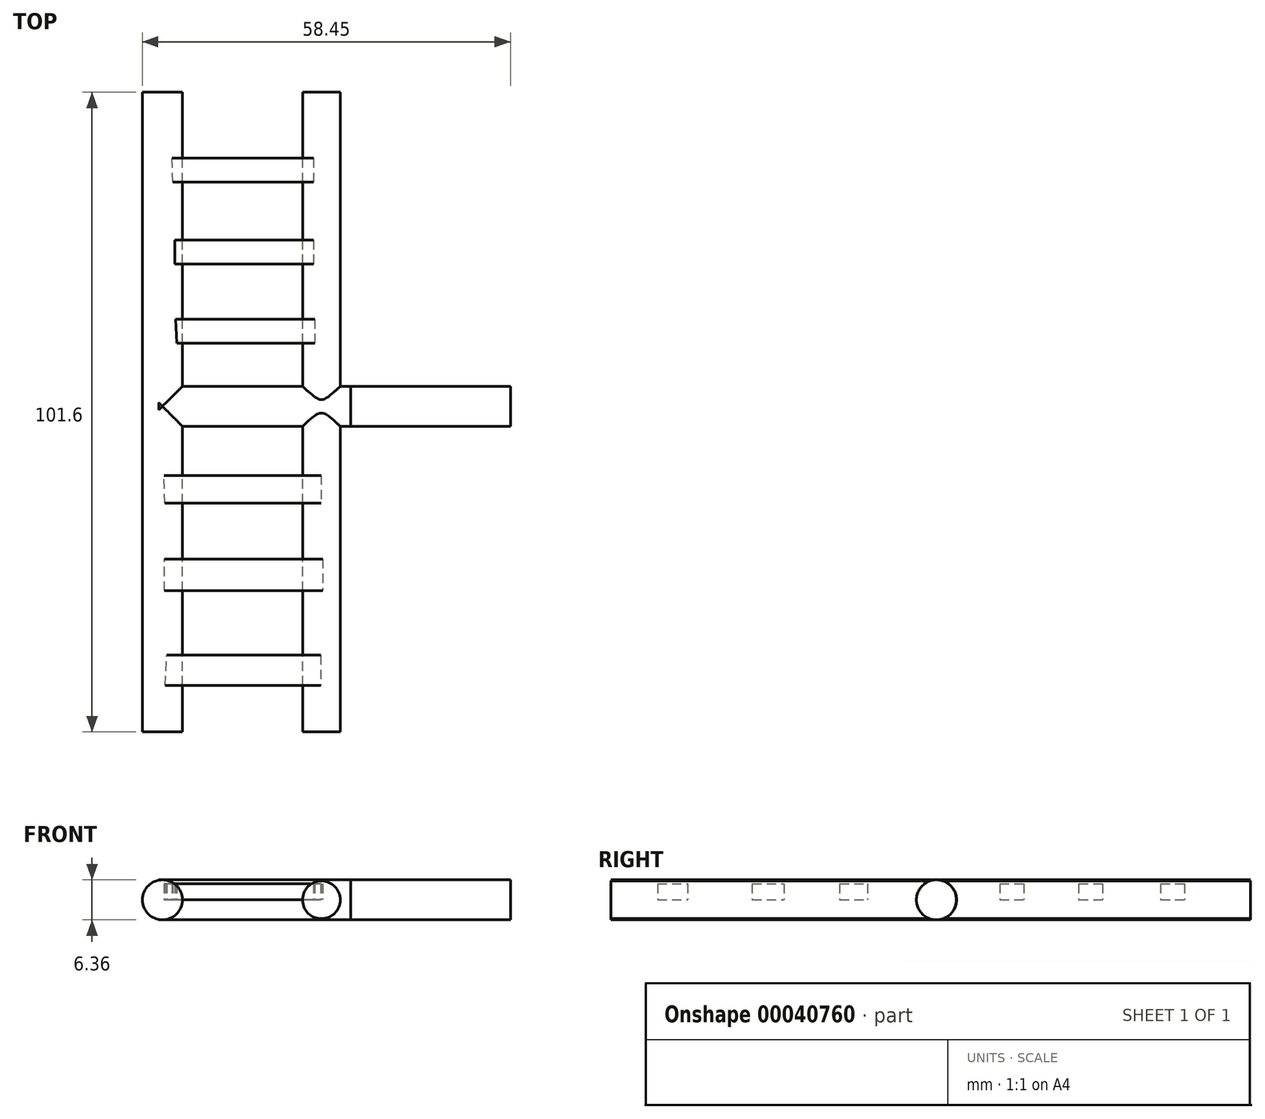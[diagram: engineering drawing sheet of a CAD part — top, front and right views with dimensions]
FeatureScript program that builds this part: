
annotation { "Feature Type Name" : "Feature", "Feature Type Description" : "" }
export const myFeature = defineFeature(function(context is Context, id is Id, definition is map)
    precondition{}
    {
        {
            var Q0;
            Q0=qCreatedBy(makeId("Front.planeOp"),FACE);
            var sketch = newSketch(context, id + "F0", { "sketchPlane" : qUnion([Q0])});
            skCircle(sketch, "E0", {"center": v(-29.87, 0) * mm, "radius": 3.18 * mm});
            skCircle(sketch, "E1", {"center": v(-4.62, 0) * mm, "radius": 3 * mm});
            skLineSegment(sketch, "E2", {"start": v(-26.7, 0) * mm, "end": v(-7.61, 0) * mm});
            skSolve(sketch);
        }
        {
            var Q0;
            Q0=makeQuery(id+"F0.imprint","IMPRINT",FACE,{"disambiguationData":[TD([[makeQuery(id+"F0.imprint","IMPRINT",EDGE,{"derivedFrom":sQuery(id+"F0.wireOp",EDGE,"E1")}),1.0]])]});
            var Q1;
            Q1=makeQuery(id+"F0.imprint","IMPRINT",FACE,{"disambiguationData":[TD([[makeQuery(id+"F0.imprint","IMPRINT",EDGE,{"derivedFrom":sQuery(id+"F0.wireOp",EDGE,"E0")}),1.0]])]});
            extrude(context, id + "F1", {"entities" : qUnion([Q0, Q1]), "depth" : 101.6 * mm});
        }
        {
            var Q0;
            Q0=qCreatedBy(makeId("Top.planeOp"),FACE);
            var sketch = newSketch(context, id + "F2", { "sketchPlane" : qUnion([Q0])});
            skLineSegment(sketch, "E3", {"start": v(-28.36, -10.5) * mm, "end": v(-5.88, -10.5) * mm});
            skLineSegment(sketch, "E4", {"start": v(-5.88, -10.5) * mm, "end": v(-5.88, -14.3) * mm});
            skLineSegment(sketch, "E5", {"start": v(-5.88, -14.3) * mm, "end": v(-28.2, -14.3) * mm});
            skLineSegment(sketch, "E6", {"start": v(-28.2, -14.3) * mm, "end": v(-28.36, -10.5) * mm});
            skSolve(sketch);
        }
        {
            var Q0;
            Q0=makeQuery(id+"F2.imprint","IMPRINT",FACE,{"disambiguationData":[TD([[makeQuery(id+"F2.imprint","IMPRINT",EDGE,{"derivedFrom":sQuery(id+"F2.wireOp",EDGE,"E3")}),-1.0]])]});
            extrude(context, id + "F3", {"entities" : qUnion([Q0]), "depth" : 2.54 * mm});
        }
        {
            var Q0;
            Q0=qCreatedBy(makeId("Top.planeOp"),FACE);
            var sketch = newSketch(context, id + "F4", { "sketchPlane" : qUnion([Q0])});
            skLineSegment(sketch, "E7", {"start": v(-27.9, -23.5) * mm, "end": v(-5.9, -23.5) * mm});
            skLineSegment(sketch, "E8", {"start": v(-5.9, -23.5) * mm, "end": v(-5.9, -27.3) * mm});
            skLineSegment(sketch, "E9", {"start": v(-5.9, -27.3) * mm, "end": v(-27.89, -27.3) * mm});
            skLineSegment(sketch, "E10", {"start": v(-27.89, -27.3) * mm, "end": v(-27.9, -23.5) * mm});
            skSolve(sketch);
        }
        {
            var Q0;
            Q0=makeQuery(id+"F4.imprint","IMPRINT",FACE,{"disambiguationData":[TD([[makeQuery(id+"F4.imprint","IMPRINT",EDGE,{"derivedFrom":sQuery(id+"F4.wireOp",EDGE,"E7")}),-1.0]])]});
            extrude(context, id + "F5", {"entities" : qUnion([Q0]), "depth" : 2.54 * mm});
        }
        {
            var Q0;
            Q0=qCreatedBy(makeId("Top.planeOp"),FACE);
            var sketch = newSketch(context, id + "F6", { "sketchPlane" : qUnion([Q0])});
            skLineSegment(sketch, "E11", {"start": v(-27.8, -36.06) * mm, "end": v(-5.7, -36.06) * mm});
            skLineSegment(sketch, "E12", {"start": v(-5.7, -36.06) * mm, "end": v(-5.7, -39.87) * mm});
            skLineSegment(sketch, "E13", {"start": v(-5.7, -39.87) * mm, "end": v(-27.57, -39.87) * mm});
            skLineSegment(sketch, "E14", {"start": v(-27.57, -39.87) * mm, "end": v(-27.8, -36.06) * mm});
            skSolve(sketch);
        }
        {
            var Q0;
            Q0 = qSketchRegion(id + "F6", true);
            extrude(context, id + "F7", {"entities" : qUnion([Q0]), "depth" : 2.54 * mm});
        }
        {
            var Q0;
            Q0=qCreatedBy(makeId("Top.planeOp"),FACE);
            var sketch = newSketch(context, id + "F8", { "sketchPlane" : qUnion([Q0])});
            skLineSegment(sketch, "E15", {"start": v(-29.64, -60.86) * mm, "end": v(-4.67, -60.86) * mm});
            skLineSegment(sketch, "E16", {"start": v(-4.67, -60.86) * mm, "end": v(-4.67, -65.29) * mm});
            skLineSegment(sketch, "E17", {"start": v(-4.67, -65.29) * mm, "end": v(-29.5, -65.29) * mm});
            skLineSegment(sketch, "E18", {"start": v(-29.5, -65.29) * mm, "end": v(-29.64, -60.86) * mm});
            skSolve(sketch);
        }
        {
            var Q0;
            Q0 = qSketchRegion(id + "F8", true);
            extrude(context, id + "F9", {"entities" : qUnion([Q0]), "depth" : 2.54 * mm});
        }
        {
            var Q0;
            Q0=qCreatedBy(makeId("Top.planeOp"),FACE);
            var sketch = newSketch(context, id + "F10", { "sketchPlane" : qUnion([Q0])});
            skLineSegment(sketch, "E19", {"start": v(-29.58, -74.15) * mm, "end": v(-4.41, -74.15) * mm});
            skLineSegment(sketch, "E20", {"start": v(-4.41, -74.15) * mm, "end": v(-4.41, -79.19) * mm});
            skLineSegment(sketch, "E21", {"start": v(-4.41, -79.19) * mm, "end": v(-29.58, -79.19) * mm});
            skLineSegment(sketch, "E22", {"start": v(-29.58, -79.19) * mm, "end": v(-29.58, -74.15) * mm});
            skSolve(sketch);
        }
        {
            var Q0;
            Q0 = qSketchRegion(id + "F10", true);
            extrude(context, id + "F11", {"entities" : qUnion([Q0]), "depth" : 2.54 * mm});
        }
        {
            var Q0;
            Q0=qCreatedBy(makeId("Top.planeOp"),FACE);
            var sketch = newSketch(context, id + "F12", { "sketchPlane" : qUnion([Q0])});
            skLineSegment(sketch, "E23", {"start": v(-29.2, -89.43) * mm, "end": v(-4.72, -89.43) * mm});
            skLineSegment(sketch, "E24", {"start": v(-4.72, -89.43) * mm, "end": v(-4.72, -94.23) * mm});
            skLineSegment(sketch, "E25", {"start": v(-4.72, -94.23) * mm, "end": v(-29.44, -94.23) * mm});
            skLineSegment(sketch, "E26", {"start": v(-29.44, -94.23) * mm, "end": v(-29.2, -89.43) * mm});
            skSolve(sketch);
        }
        {
            var Q0;
            Q0 = qSketchRegion(id + "F12", true);
            extrude(context, id + "F13", {"entities" : qUnion([Q0]), "depth" : 2.54 * mm});
        }
        {
            var Q0;
            Q0=qCreatedBy(makeId("Right.planeOp"),FACE);
            var sketch = newSketch(context, id + "F14", { "sketchPlane" : qUnion([Q0])});
            skCircle(sketch, "E27", {"center": v(-49.91, 0) * mm, "radius": 3.18 * mm});
            skSolve(sketch);
        }
        {
            var Q0;
            Q0 = qSketchRegion(id + "F14", true);
            extrude(context, id + "F15", {"entities" : qUnion([Q0]), "depth" : 25.4 * mm});
        }
        {
            var Q0;
            Q0=qCreatedBy(makeId("Right.planeOp"),FACE);
            var sketch = newSketch(context, id + "F16", { "sketchPlane" : qUnion([Q0])});
            skCircle(sketch, "E28", {"center": v(-49.9, 0) * mm, "radius": 3.18 * mm});
            skSolve(sketch);
        }
        {
            var Q0;
            Q0 = qSketchRegion(id + "F16", true);
            extrude(context, id + "F17", {"entities" : qUnion([Q0]), "operationType" : NewBodyOperationType.ADD, "oppositeDirection" : true, "depth" : 30.48 * mm});
        }
    });
